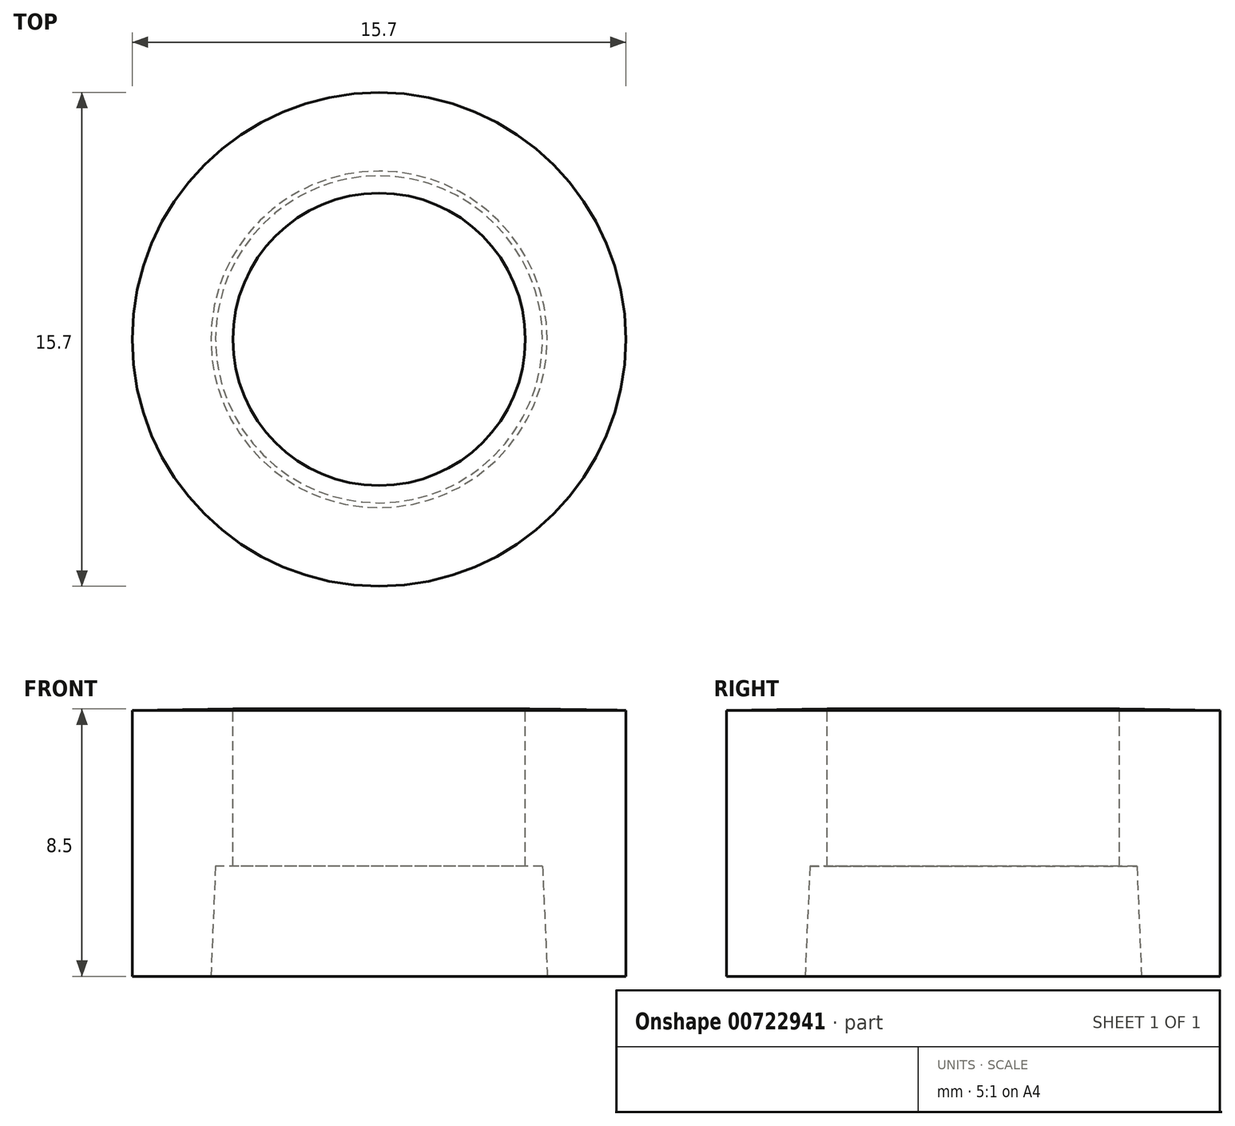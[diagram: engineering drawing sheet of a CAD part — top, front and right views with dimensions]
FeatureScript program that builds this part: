
annotation { "Feature Type Name" : "Feature", "Feature Type Description" : "" }
export const myFeature = defineFeature(function(context is Context, id is Id, definition is map)
    precondition{}
    {
        {
            var Q0;
            Q0=qCreatedBy(makeId("Front.planeOp"),FACE);
            var sketch = newSketch(context, id + "F0", { "sketchPlane" : qUnion([Q0])});
            skLineSegment(sketch, "E0", {"start": v(4.65, 3.5) * mm, "end": v(4.65, 8.5) * mm});
            skLineSegment(sketch, "E1", {"start": v(5.2, 3.5) * mm, "end": v(5.35, 0) * mm});
            skLineSegment(sketch, "E2", {"start": v(4.65, 3.5) * mm, "end": v(5.2, 3.5) * mm});
            skLineSegment(sketch, "E3", {"start": v(5.35, 0) * mm, "end": v(7.85, 0) * mm});
            skLineSegment(sketch, "E4", {"start": v(7.85, 0) * mm, "end": v(7.85, 8.46) * mm});
            skLineSegment(sketch, "E5", {"start": v(7.85, 8.46) * mm, "end": v(4.65, 8.5) * mm});
            skSolve(sketch);
        }
        {
            var Q0;
            Q0=qCreatedBy(makeId("Front.planeOp"),FACE);
            var sketch = newSketch(context, id + "F1", { "sketchPlane" : qUnion([Q0])});
            skLineSegment(sketch, "E6", {"start": v(0, 22.38) * mm, "end": v(0, -15) * mm});
            skSolve(sketch);
        }
        {
            var Q0;
            Q0=makeQuery(id+"F0.imprint","IMPRINT",FACE,{"disambiguationData":[TD([[makeQuery(id+"F0.imprint","IMPRINT",EDGE,{"derivedFrom":sQuery(id+"F0.wireOp",EDGE,"E0")}),-1.0]])]});
            var Q1;
            Q1=sQuery(id+"F1.wireOp",EDGE,"E6");
            revolve(context, id + "F2", {"surfaceOperationType" : NewSurfaceOperationType.NEW, "entities" : qUnion([Q0]), "axis" : qUnion([Q1]), "revolveType" : RevolveType.FULL});
        }
    });
